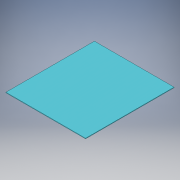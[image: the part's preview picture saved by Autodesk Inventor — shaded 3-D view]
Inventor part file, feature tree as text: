
AUTODESK INVENTOR PART (.ipt)
format: ipt  version: 2017 (Build 210142000, 142)  size: 91,648 bytes
history: native  units: in
note: dims shown in document units (in); Inventor stores cm internally (conversion verified against a paired STEP export)
features: extrude x1, sketch x1
ambient origin geometry x8: Origin, YZ Plane, XZ Plane, XY Plane, X Axis, Y Axis, Z Axis, Center Point
bodies: Solid1 (feature_tree)
feature tree (2):
  extrude  "Extrusion1"  Depth=20.0in
  sketch  "Sketch1"  dims[d0=18.0in d1=20.0in d2=18.0in d3=0.125in d4=0.0in]
